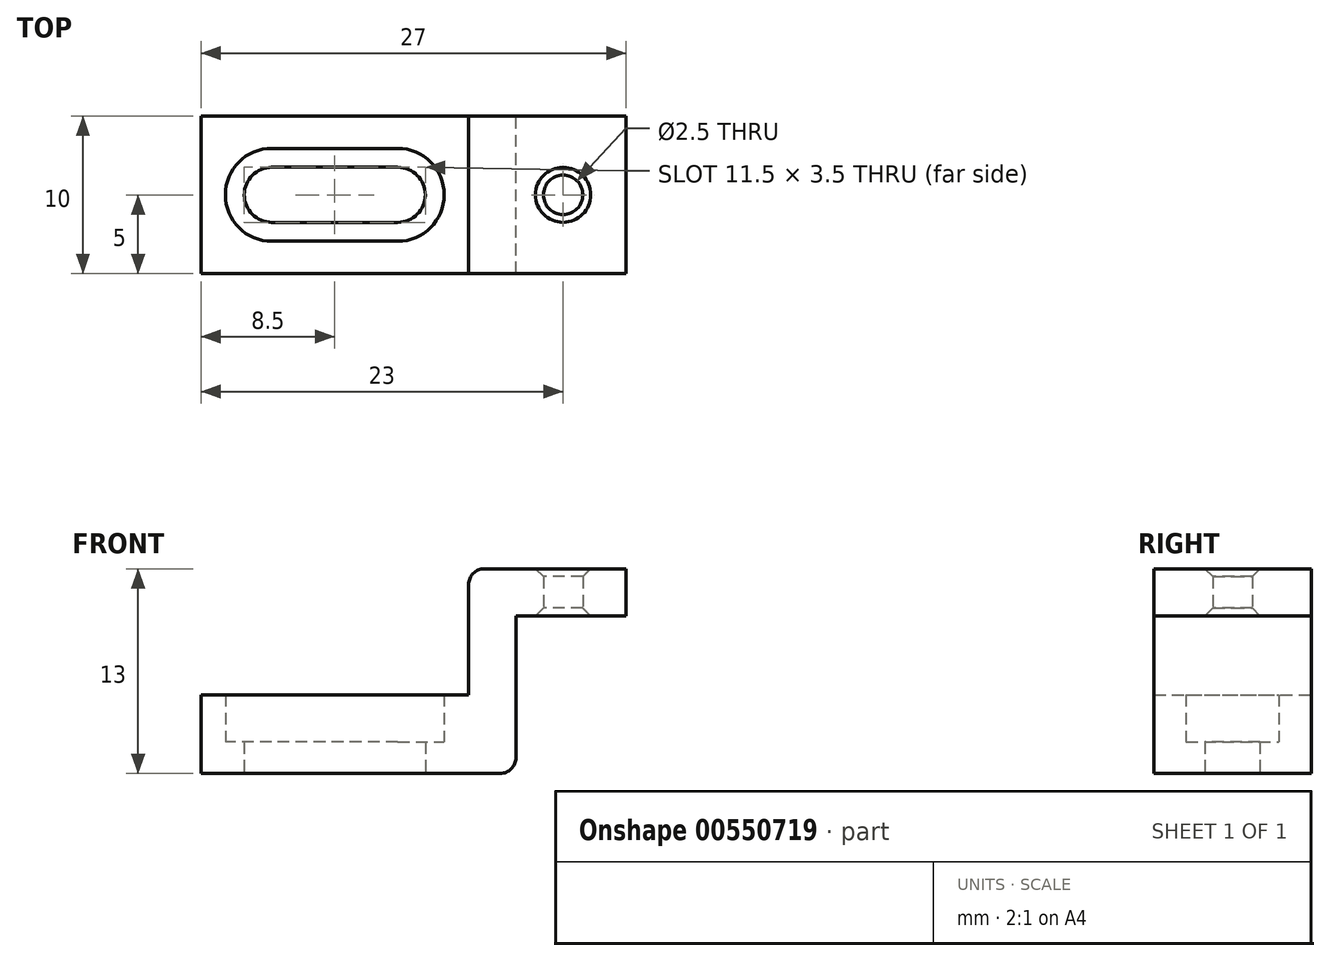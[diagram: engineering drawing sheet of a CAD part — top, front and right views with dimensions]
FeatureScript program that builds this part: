
annotation { "Feature Type Name" : "Feature", "Feature Type Description" : "" }
export const myFeature = defineFeature(function(context is Context, id is Id, definition is map)
    precondition{}
    {
        {
            var Q0;
            Q0=qCreatedBy(makeId("Top.planeOp"),FACE);
            var sketch = newSketch(context, id + "F0", { "sketchPlane" : qUnion([Q0])});
            skLineSegment(sketch, "E0.rect.bottom", {"start": v(8.5, -5) * mm, "end": v(-8.5, -5) * mm});
            skLineSegment(sketch, "E0.rect.top", {"start": v(8.5, 5) * mm, "end": v(-8.5, 5) * mm});
            skLineSegment(sketch, "E0.rect.left", {"start": v(8.5, -5) * mm, "end": v(8.5, 5) * mm});
            skLineSegment(sketch, "E0.rect.right", {"start": v(-8.5, -5) * mm, "end": v(-8.5, 5) * mm});
            skPoint(sketch, "E0.rect.middle", {"position": v(0, 0) * mm});
            skLineSegment(sketch, "E1.rect.bottom", {"start": v(-4, 1.75) * mm, "end": v(4, 1.75) * mm});
            skLineSegment(sketch, "E1.rect.top", {"start": v(-4, -1.75) * mm, "end": v(4, -1.75) * mm});
            skLineSegment(sketch, "E1.rect.left", {"start": v(-4, 1.75) * mm, "end": v(-4, -1.75) * mm});
            skLineSegment(sketch, "E1.rect.right", {"start": v(4, 1.75) * mm, "end": v(4, -1.75) * mm});
            skCircle(sketch, "E2", {"center": v(-4, 0) * mm, "radius": 1.75 * mm});
            skCircle(sketch, "E3", {"center": v(4, 0) * mm, "radius": 1.75 * mm});
            skLineSegment(sketch, "E4.rect.bottom", {"start": v(4, -2.95) * mm, "end": v(-4, -2.95) * mm});
            skLineSegment(sketch, "E4.rect.top", {"start": v(4, 2.95) * mm, "end": v(-4, 2.95) * mm});
            skLineSegment(sketch, "E4.rect.left", {"start": v(4, -2.95) * mm, "end": v(4, 2.95) * mm});
            skLineSegment(sketch, "E4.rect.right", {"start": v(-4, -2.95) * mm, "end": v(-4, 2.95) * mm});
            skCircle(sketch, "E5", {"center": v(-4, 0) * mm, "radius": 2.95 * mm});
            skCircle(sketch, "E6", {"center": v(4, 0) * mm, "radius": 2.95 * mm});
            skLineSegment(sketch, "E7", {"start": v(0, 2.95) * mm, "end": v(0, -2.95) * mm, "construction": true});
            skSolve(sketch);
        }
        {
            var Q0;
            Q0=qSketchRegion(id+"F0",true);
            extrude(context, id + "F1", {"entities" : qUnion([Q0]), "depth" : 5 * mm});
        }
        {
            var Q0;
            {var subQ1=sQuery(id+"F0.wireOp",EDGE,"E4.rect.right");var subQ4=sQuery(id+"F0.wireOp",EDGE,"E2");var subQ5=makeQuery(id+"F0.imprint","INTERSECT",VERTEX,{"derivedFrom":[sQuery(id+"F0.wireOp",EDGE,"E1.rect.bottom"),subQ4,subQ1]});Q0=makeQuery(id+"F0.imprint","IMPRINT",FACE,{"disambiguationData":[TD([[makeQuery(id+"F0.imprint","IMPRINT",EDGE,{"disambiguationData":[TD([[subQ5,-1.0]])],"derivedFrom":subQ4}),-1.0]])]});}
            var Q1;
            {var subQ0=sQuery(id+"F0.wireOp",EDGE,"E5");var subQ1=sQuery(id+"F0.wireOp",EDGE,"E1.rect.bottom");var subQ2=makeQuery(id+"F0.imprint","INTERSECT",VERTEX,{"derivedFrom":[subQ1,subQ0]});Q1=makeQuery(id+"F0.imprint","IMPRINT",FACE,{"disambiguationData":[TD([[makeQuery(id+"F0.imprint","IMPRINT",EDGE,{"disambiguationData":[TD([[subQ2,1.0]])],"derivedFrom":subQ1}),1.0]])]});}
            var Q2;
            {var subQ3=sQuery(id+"F0.wireOp",EDGE,"E4.rect.top");Q2=makeQuery(id+"F0.imprint","IMPRINT",FACE,{"disambiguationData":[TD([[makeQuery(id+"F0.imprint","IMPRINT",EDGE,{"derivedFrom":subQ3}),1.0]])]});}
            var Q3;
            {var subQ0=sQuery(id+"F0.wireOp",EDGE,"E6");var subQ1=sQuery(id+"F0.wireOp",EDGE,"E1.rect.bottom");var subQ2=makeQuery(id+"F0.imprint","INTERSECT",VERTEX,{"derivedFrom":[subQ1,subQ0]});Q3=makeQuery(id+"F0.imprint","IMPRINT",FACE,{"disambiguationData":[TD([[makeQuery(id+"F0.imprint","IMPRINT",EDGE,{"disambiguationData":[TD([[subQ2,-1.0]])],"derivedFrom":subQ1}),1.0]])]});}
            var Q4;
            {var subQ1=sQuery(id+"F0.wireOp",EDGE,"E4.rect.left");var subQ4=sQuery(id+"F0.wireOp",EDGE,"E3");var subQ5=makeQuery(id+"F0.imprint","INTERSECT",VERTEX,{"derivedFrom":[sQuery(id+"F0.wireOp",EDGE,"E1.rect.bottom"),subQ4,subQ1]});Q4=makeQuery(id+"F0.imprint","IMPRINT",FACE,{"disambiguationData":[TD([[makeQuery(id+"F0.imprint","IMPRINT",EDGE,{"disambiguationData":[TD([[subQ5,1.0]])],"derivedFrom":subQ4}),-1.0]])]});}
            var Q5;
            {var subQ0=sQuery(id+"F0.wireOp",EDGE,"E6");var subQ1=sQuery(id+"F0.wireOp",EDGE,"E1.rect.top");var subQ2=makeQuery(id+"F0.imprint","INTERSECT",VERTEX,{"derivedFrom":[subQ1,subQ0]});Q5=makeQuery(id+"F0.imprint","IMPRINT",FACE,{"disambiguationData":[TD([[makeQuery(id+"F0.imprint","IMPRINT",EDGE,{"disambiguationData":[TD([[subQ2,-1.0]])],"derivedFrom":subQ1}),-1.0]])]});}
            var Q6;
            {var subQ3=sQuery(id+"F0.wireOp",EDGE,"E4.rect.bottom");Q6=makeQuery(id+"F0.imprint","IMPRINT",FACE,{"disambiguationData":[TD([[makeQuery(id+"F0.imprint","IMPRINT",EDGE,{"derivedFrom":subQ3}),-1.0]])]});}
            var Q7;
            {var subQ0=sQuery(id+"F0.wireOp",EDGE,"E5");var subQ1=sQuery(id+"F0.wireOp",EDGE,"E1.rect.top");var subQ2=makeQuery(id+"F0.imprint","INTERSECT",VERTEX,{"derivedFrom":[subQ1,subQ0]});Q7=makeQuery(id+"F0.imprint","IMPRINT",FACE,{"disambiguationData":[TD([[makeQuery(id+"F0.imprint","IMPRINT",EDGE,{"disambiguationData":[TD([[subQ2,1.0]])],"derivedFrom":subQ1}),-1.0]])]});}
            extrude(context, id + "F2", {"entities" : qUnion([Q0, Q1, Q2, Q3, Q4, Q5, Q6, Q7]), "operationType" : NewBodyOperationType.ADD, "depth" : 2 * mm});
        }
        {
            var Q0;
            Q0=makeQuery(id+"F1.opExtrude","SWEPT_FACE",FACE,{"disambiguationData":[OSD([sQuery(id+"F0.wireOp",EDGE,"E0.rect.left")])]});
            var sketch = newSketch(context, id + "F3", { "sketchPlane" : qUnion([Q0])});
            skLineSegment(sketch, "E8.bottom", {"start": v(-5, 0) * mm, "end": v(5, 0) * mm});
            skLineSegment(sketch, "E8.top", {"start": v(-5, 10) * mm, "end": v(5, 10) * mm});
            skLineSegment(sketch, "E8.left", {"start": v(-5, 0) * mm, "end": v(-5, 10) * mm});
            skLineSegment(sketch, "E8.right", {"start": v(5, 0) * mm, "end": v(5, 10) * mm});
            skSolve(sketch);
        }
        {
            var Q0;
            Q0=qSketchRegion(id+"F3",true);
            extrude(context, id + "F4", {"entities" : qUnion([Q0]), "operationType" : NewBodyOperationType.ADD, "depth" : 3 * mm});
        }
        {
            var Q0;
            Q0=makeQuery(id+"F4.opExtrude","SWEPT_FACE",FACE,{"disambiguationData":[OSD([sQuery(id+"F3.wireOp",EDGE,"E8.top")])]});
            var sketch = newSketch(context, id + "F5", { "sketchPlane" : qUnion([Q0])});
            skLineSegment(sketch, "E9.bottom", {"start": v(8.5, 5) * mm, "end": v(18.5, 5) * mm});
            skLineSegment(sketch, "E9.top", {"start": v(8.5, -5) * mm, "end": v(18.5, -5) * mm});
            skLineSegment(sketch, "E9.left", {"start": v(8.5, 5) * mm, "end": v(8.5, -5) * mm});
            skLineSegment(sketch, "E9.right", {"start": v(18.5, 5) * mm, "end": v(18.5, -5) * mm});
            skCircle(sketch, "E10", {"center": v(14.5, 0) * mm, "radius": 1.25 * mm});
            skCircle(sketch, "E11", {"center": v(14.5, 0) * mm, "radius": 1.75 * mm, "construction": true});
            skSolve(sketch);
        }
        {
            var Q0;
            Q0=qSketchRegion(id+"F5",true);
            extrude(context, id + "F6", {"entities" : qUnion([Q0]), "operationType" : NewBodyOperationType.ADD, "depth" : 3 * mm});
        }
        {
            var Q0;
            Q0=makeQuery(id+"F6.opExtrude","CAP_EDGE",EDGE,{"disambiguationData":[OSD([sQuery(id+"F5.wireOp",EDGE,"E9.left")])],"isStart":false});
            var Q1;
            Q1=makeQuery(id+"F4.opExtrude","CAP_EDGE",EDGE,{"disambiguationData":[OSD([sQuery(id+"F3.wireOp",EDGE,"E8.top")])],"isStart":false});
            var Q2;
            Q2=makeQuery(id+"F4.opExtrude","CAP_EDGE",EDGE,{"disambiguationData":[OSD([sQuery(id+"F3.wireOp",EDGE,"E8.bottom")])],"isStart":false});
            var Q3;
            Q3=makeQuery(id+"F1.opExtrude","CAP_EDGE",EDGE,{"disambiguationData":[OSD([sQuery(id+"F0.wireOp",EDGE,"E0.rect.left")])],"isStart":false});
            fillet(context, id + "F7", {"entities" : qUnion([Q0, Q1, Q2, Q3]), "radius" : 1 * mm, "tangentPropagation" : true, "allowEdgeOverflow" : false});
        }
        {
            var Q0;
            Q0=makeQuery(id+"F6.opExtrude","SWEPT_FACE",FACE,{"disambiguationData":[OSD([sQuery(id+"F5.wireOp",EDGE,"E10")])]});
            chamfer(context, id + "F8", {"entities" : qUnion([Q0]), "width" : 0.5 * mm, "tangentPropagation" : true});
        }
    });
